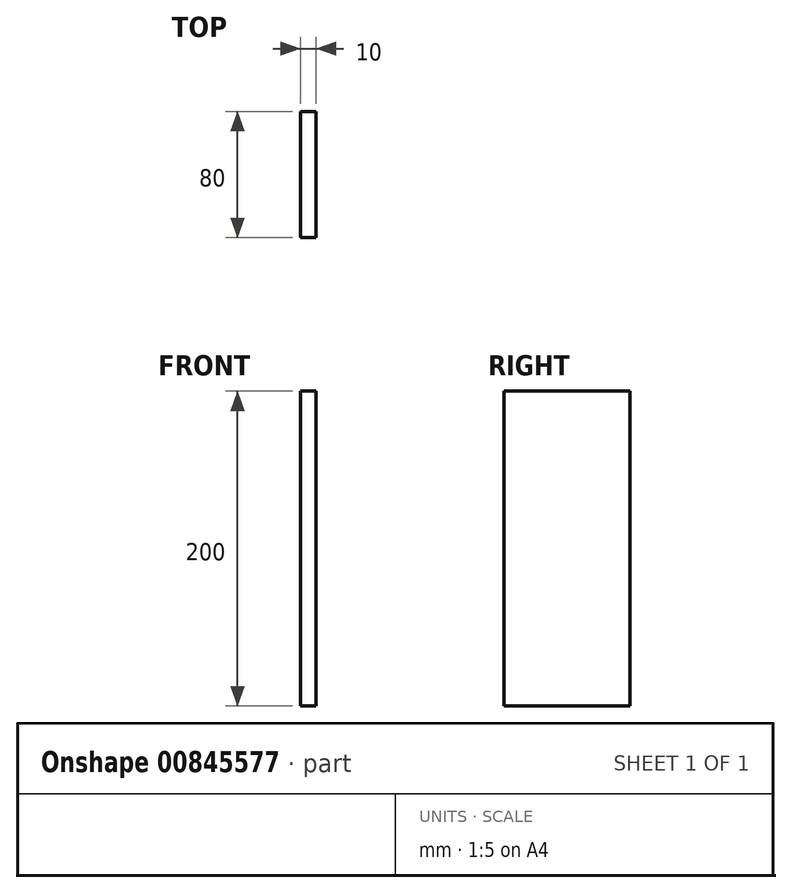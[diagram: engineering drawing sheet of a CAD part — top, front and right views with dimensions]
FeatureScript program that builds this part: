
annotation { "Feature Type Name" : "Feature", "Feature Type Description" : "" }
export const myFeature = defineFeature(function(context is Context, id is Id, definition is map)
    precondition{}
    {
        {
            var Q0;
            Q0=qCreatedBy(makeId("Right.planeOp"),FACE);
            var sketch = newSketch(context, id + "F0", { "sketchPlane" : qUnion([Q0])});
            skLineSegment(sketch, "E0.bottom", {"start": v(-40.66, 123.9) * mm, "end": v(39.34, 123.9) * mm});
            skLineSegment(sketch, "E0.top", {"start": v(-40.66, -76.1) * mm, "end": v(39.34, -76.1) * mm});
            skLineSegment(sketch, "E0.left", {"start": v(-40.66, 123.9) * mm, "end": v(-40.66, -76.1) * mm});
            skLineSegment(sketch, "E0.right", {"start": v(39.34, 123.9) * mm, "end": v(39.34, -76.1) * mm});
            skSolve(sketch);
        }
        {
            var Q0;
            Q0=makeQuery(id+"F0.imprint","IMPRINT",FACE,{"disambiguationData":[TD([[makeQuery(id+"F0.imprint","IMPRINT",EDGE,{"derivedFrom":sQuery(id+"F0.wireOp",EDGE,"E0.bottom")}),-1.0]])]});
            extrude(context, id + "F1", {"entities" : qUnion([Q0]), "depth" : 10 * mm, "offsetDistance" : 25 * mm});
        }
    });
